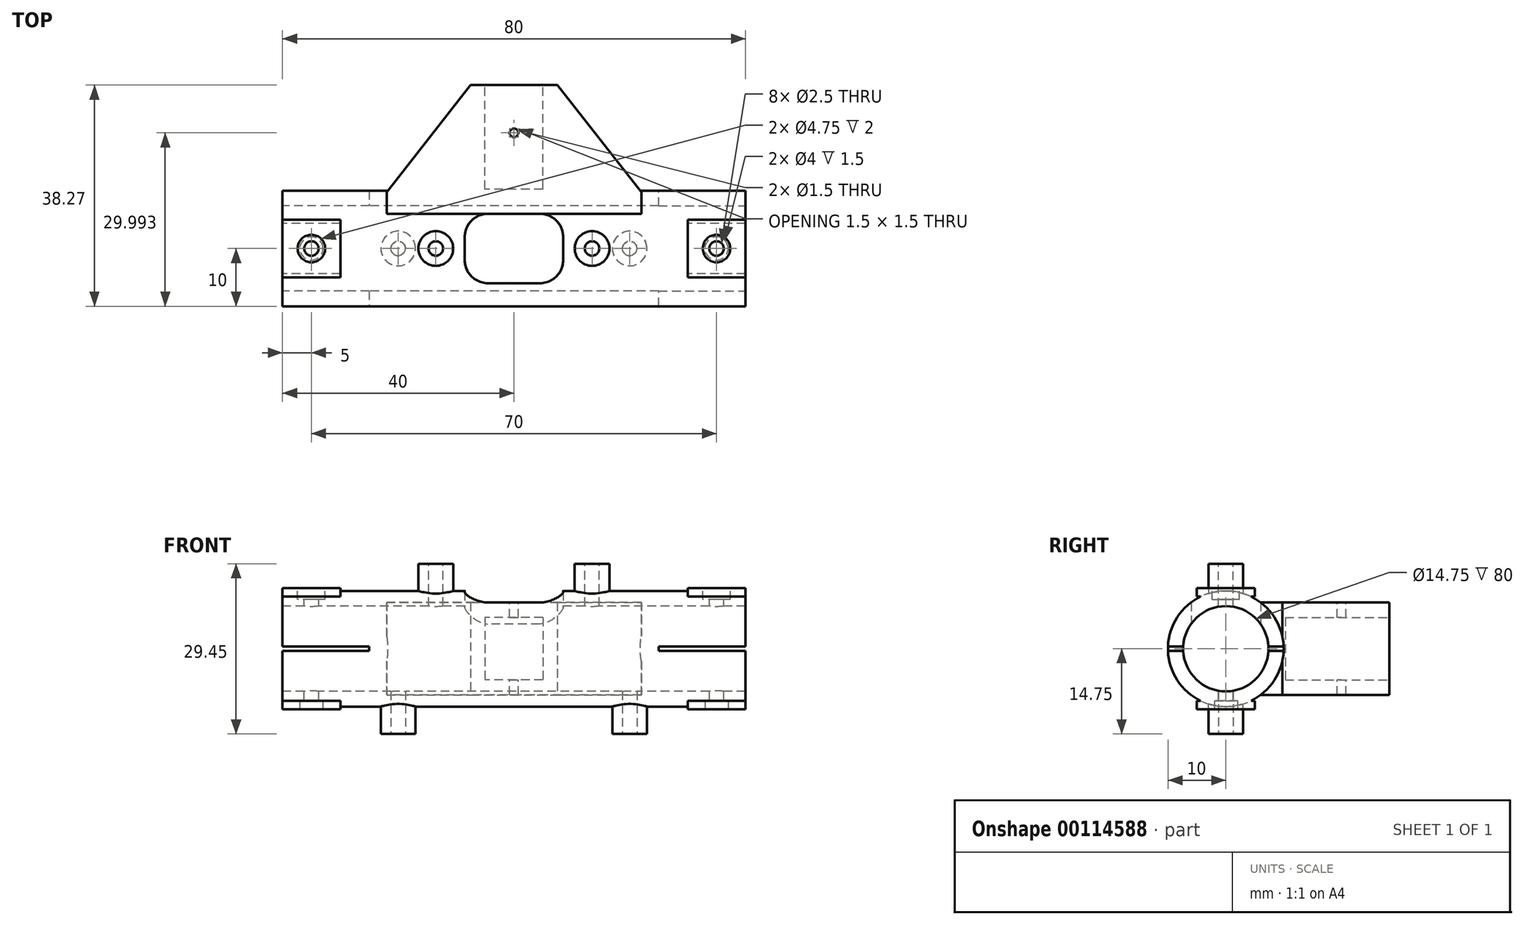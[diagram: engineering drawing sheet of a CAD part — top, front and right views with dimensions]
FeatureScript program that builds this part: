
annotation { "Feature Type Name" : "Feature", "Feature Type Description" : "" }
export const myFeature = defineFeature(function(context is Context, id is Id, definition is map)
    precondition{}
    {
        {
            var Q0;
            Q0=qCreatedBy(makeId("Right.planeOp"),FACE);
            var sketch = newSketch(context, id + "F0", { "sketchPlane" : qUnion([Q0])});
            skCircle(sketch, "E0", {"center": v(0, 0) * mm, "radius": 7.38 * mm});
            skCircle(sketch, "E1", {"center": v(0, 0) * mm, "radius": 10 * mm});
            skSolve(sketch);
        }
        {
            var Q0;
            Q0=makeQuery(id+"F0.imprint","IMPRINT",FACE,{"disambiguationData":[TD([[makeQuery(id+"F0.imprint","IMPRINT",EDGE,{"derivedFrom":sQuery(id+"F0.wireOp",EDGE,"E0")}),-1.0]])]});
            extrude(context, id + "F1", {"entities" : qUnion([Q0]), "endBound" : BoundingType.SYMMETRIC, "depth" : 80 * mm});
        }
        {
            var Q0;
            Q0=qCreatedBy(makeId("Top.planeOp"),FACE);
            var sketch = newSketch(context, id + "F2", { "sketchPlane" : qUnion([Q0])});
            skLineSegment(sketch, "E2", {"start": v(-22, 9.77) * mm, "end": v(-7.5, 28.27) * mm});
            skLineSegment(sketch, "E3", {"start": v(-7.5, 28.27) * mm, "end": v(7.5, 28.27) * mm});
            skLineSegment(sketch, "E4", {"start": v(7.5, 28.27) * mm, "end": v(22, 9.77) * mm});
            skLineSegment(sketch, "E5", {"start": v(-22, 9.77) * mm, "end": v(22, 9.77) * mm});
            skSolve(sketch);
        }
        {
            var Q0;
            Q0=makeQuery(id+"F2.imprint","IMPRINT",FACE,{"disambiguationData":[TD([[makeQuery(id+"F2.imprint","IMPRINT",EDGE,{"derivedFrom":sQuery(id+"F2.wireOp",EDGE,"E2")}),-1.0]])]});
            extrude(context, id + "F3", {"entities" : qUnion([Q0]), "operationType" : NewBodyOperationType.ADD, "endBound" : BoundingType.SYMMETRIC, "depth" : 16 * mm});
        }
        {
            var Q0;
            {var subQ0=sQuery(id+"F2.wireOp",EDGE,"E2");var subQ1=sQuery(id+"F2.wireOp",EDGE,"E5");var subQ2=sQuery(id+"F2.wireOp",EDGE,"E4");Q0=makeQuery(id+"F3.boolean.opBoolean","SPLIT",FACE,{"disambiguationData":[TD([makeQuery(id+"F3.opExtrude","CAP_FACE",FACE,{"disambiguationData":[OSD([subQ0,sQuery(id+"F2.wireOp",EDGE,"E3"),subQ2,subQ1])],"isStart":false})])],"derivedFrom":makeQuery(id+"F3.opExtrude","SWEPT_FACE",FACE,{"disambiguationData":[OSD([subQ1])]})});}
            var sketch = newSketch(context, id + "F4", { "sketchPlane" : qUnion([Q0])});
            skLineSegment(sketch, "E6.bottom", {"start": v(22, 2.15) * mm, "end": v(-22, 2.15) * mm});
            skLineSegment(sketch, "E6.top", {"start": v(22, 8) * mm, "end": v(-22, 8) * mm});
            skLineSegment(sketch, "E6.left", {"start": v(22, 2.15) * mm, "end": v(22, 8) * mm});
            skLineSegment(sketch, "E6.right", {"start": v(-22, 2.15) * mm, "end": v(-22, 8) * mm});
            skSolve(sketch);
        }
        {
            var Q0;
            {var subQ0=sQuery(id+"F2.wireOp",EDGE,"E2");var subQ1=sQuery(id+"F2.wireOp",EDGE,"E5");var subQ2=sQuery(id+"F2.wireOp",EDGE,"E4");Q0=makeQuery(id+"F3.boolean.opBoolean","SPLIT",FACE,{"disambiguationData":[TD([makeQuery(id+"F3.opExtrude","CAP_FACE",FACE,{"disambiguationData":[OSD([subQ0,sQuery(id+"F2.wireOp",EDGE,"E3"),subQ2,subQ1])],"isStart":true})])],"derivedFrom":makeQuery(id+"F3.opExtrude","SWEPT_FACE",FACE,{"disambiguationData":[OSD([subQ1])]})});}
            var sketch = newSketch(context, id + "F5", { "sketchPlane" : qUnion([Q0])});
            skLineSegment(sketch, "E7.bottom", {"start": v(22, -2.15) * mm, "end": v(-22, -2.15) * mm});
            skLineSegment(sketch, "E7.top", {"start": v(22, -8) * mm, "end": v(-22, -8) * mm});
            skLineSegment(sketch, "E7.left", {"start": v(22, -2.15) * mm, "end": v(22, -8) * mm});
            skLineSegment(sketch, "E7.right", {"start": v(-22, -2.15) * mm, "end": v(-22, -8) * mm});
            skSolve(sketch);
        }
        {
            var Q0;
            Q0=makeQuery(id+"F4.imprint","IMPRINT",FACE,{"disambiguationData":[TD([[makeQuery(id+"F4.imprint","IMPRINT",EDGE,{"derivedFrom":sQuery(id+"F4.wireOp",EDGE,"E6.bottom")}),1.0]])]});
            var Q1;
            Q1=makeQuery(id+"F5.imprint","IMPRINT",FACE,{"disambiguationData":[TD([[makeQuery(id+"F5.imprint","IMPRINT",EDGE,{"derivedFrom":sQuery(id+"F5.wireOp",EDGE,"E7.bottom")}),1.0]])]});
            extrude(context, id + "F6", {"entities" : qUnion([Q0, Q1]), "operationType" : NewBodyOperationType.ADD, "depth" : 10 * mm});
        }
        {
            var Q0;
            Q0=makeQuery(id+"F3.opExtrude","SWEPT_FACE",FACE,{"disambiguationData":[OSD([sQuery(id+"F2.wireOp",EDGE,"E3")])]});
            var sketch = newSketch(context, id + "F7", { "sketchPlane" : qUnion([Q0])});
            skLineSegment(sketch, "E8.bottom", {"start": v(-5, 5.38) * mm, "end": v(5, 5.38) * mm});
            skLineSegment(sketch, "E8.top", {"start": v(-5, -5.38) * mm, "end": v(5, -5.38) * mm});
            skLineSegment(sketch, "E8.left", {"start": v(-5, 5.38) * mm, "end": v(-5, -5.38) * mm});
            skLineSegment(sketch, "E8.right", {"start": v(5, 5.38) * mm, "end": v(5, -5.38) * mm});
            skPoint(sketch, "E8.middle", {"position": v(0, 0) * mm});
            skPoint(sketch, "E8.middle.positionSnap0", {"position": v(0, 8) * mm});
            skPoint(sketch, "E8.middle.positionSnap1", {"position": v(-7.5, 0) * mm});
            skPoint(sketch, "E8.centerSnap0", {"position": v(0, 8) * mm});
            skPoint(sketch, "E8.centerSnap1", {"position": v(-7.5, 0) * mm});
            skSolve(sketch);
        }
        {
            var Q0;
            Q0=makeQuery(id+"F7.imprint","IMPRINT",FACE,{"disambiguationData":[TD([[makeQuery(id+"F7.imprint","IMPRINT",EDGE,{"derivedFrom":sQuery(id+"F7.wireOp",EDGE,"E8.bottom")}),-1.0]])]});
            extrude(context, id + "F8", {"entities" : qUnion([Q0]), "operationType" : NewBodyOperationType.REMOVE, "oppositeDirection" : true, "depth" : 18 * mm});
        }
        {
            var Q0;
            Q0=qCreatedBy(makeId("Top.planeOp"),FACE);
            cPlane(context, id + "F9", {"entities" : qUnion([Q0]), "cplaneType" : CPlaneType.OFFSET, "offset" : 9 * mm, "width" : 150 * mm, "height" : 150 * mm});
        }
        {
            var Q0;
            Q0=qCreatedBy(id+"F9.planeOp",FACE);
            var sketch = newSketch(context, id + "F10", { "sketchPlane" : qUnion([Q0])});
            skLineSegment(sketch, "E9.bottom", {"start": v(-40, 5) * mm, "end": v(-30, 5) * mm});
            skLineSegment(sketch, "E9.top", {"start": v(-40, -5) * mm, "end": v(-30, -5) * mm});
            skLineSegment(sketch, "E9.left", {"start": v(-40, 5) * mm, "end": v(-40, -5) * mm});
            skLineSegment(sketch, "E9.right", {"start": v(-30, 5) * mm, "end": v(-30, -5) * mm});
            skLineSegment(sketch, "E10.MirrorCS", {"start": v(40, 5) * mm, "end": v(30, 5) * mm});
            skLineSegment(sketch, "E11.MirrorCS", {"start": v(40, -5) * mm, "end": v(30, -5) * mm});
            skLineSegment(sketch, "E12.MirrorCS", {"start": v(30, 5) * mm, "end": v(30, -5) * mm});
            skLineSegment(sketch, "E13.MirrorCS", {"start": v(40, 5) * mm, "end": v(40, -5) * mm});
            skSolve(sketch);
        }
        {
            var Q0;
            Q0 = qSketchRegion(id + "F10", true);
            extrude(context, id + "F11", {"entities" : qUnion([Q0]), "operationType" : NewBodyOperationType.ADD, "depth" : 1.5 * mm});
        }
        {
            var Q0;
            Q0=qCreatedBy(makeId("Top.planeOp"),FACE);
            cPlane(context, id + "F12", {"entities" : qUnion([Q0]), "cplaneType" : CPlaneType.OFFSET, "offset" : 9 * mm, "oppositeDirection" : true, "width" : 150 * mm, "height" : 150 * mm});
        }
        {
            var Q0;
            Q0=qCreatedBy(id+"F12.planeOp",FACE);
            var sketch = newSketch(context, id + "F13", { "sketchPlane" : qUnion([Q0])});
            skLineSegment(sketch, "E14.bottom", {"start": v(-40, -5) * mm, "end": v(-30, -5) * mm});
            skLineSegment(sketch, "E14.top", {"start": v(-40, 5) * mm, "end": v(-30, 5) * mm});
            skLineSegment(sketch, "E14.left", {"start": v(-40, -5) * mm, "end": v(-40, 5) * mm});
            skLineSegment(sketch, "E14.right", {"start": v(-30, -5) * mm, "end": v(-30, 5) * mm});
            skLineSegment(sketch, "E15.MirrorCS", {"start": v(30, -5) * mm, "end": v(30, 5) * mm});
            skLineSegment(sketch, "E16.MirrorCS", {"start": v(40, -5) * mm, "end": v(40, 5) * mm});
            skLineSegment(sketch, "E17.MirrorCS", {"start": v(40, -5) * mm, "end": v(30, -5) * mm});
            skLineSegment(sketch, "E18.MirrorCS", {"start": v(40, 5) * mm, "end": v(30, 5) * mm});
            skSolve(sketch);
        }
        {
            var Q0;
            Q0 = qSketchRegion(id + "F13", true);
            extrude(context, id + "F14", {"entities" : qUnion([Q0]), "operationType" : NewBodyOperationType.ADD, "oppositeDirection" : true, "depth" : 1.5 * mm});
        }
        {
            var Q0;
            Q0=qCreatedBy(id+"F9.planeOp",FACE);
            var sketch = newSketch(context, id + "F15", { "sketchPlane" : qUnion([Q0])});
            skCircle(sketch, "E19", {"center": v(-13.5, 0) * mm, "radius": 3 * mm});
            skCircle(sketch, "E20.MirrorC", {"center": v(13.5, 0) * mm, "radius": 3 * mm});
            skSolve(sketch);
        }
        {
            var Q0;
            Q0 = qSketchRegion(id + "F15", true);
            extrude(context, id + "F16", {"entities" : qUnion([Q0]), "operationType" : NewBodyOperationType.ADD, "depth" : 5.7 * mm});
        }
        {
            var Q0;
            Q0=makeQuery(id+"F11.opExtrude","CAP_FACE",FACE,{"disambiguationData":[OSD([sQuery(id+"F10.wireOp",EDGE,"E9.bottom"),sQuery(id+"F10.wireOp",EDGE,"E9.top"),sQuery(id+"F10.wireOp",EDGE,"E9.left"),sQuery(id+"F10.wireOp",EDGE,"E9.right")])],"isStart":false});
            var sketch = newSketch(context, id + "F17", { "sketchPlane" : qUnion([Q0])});
            skPoint(sketch, "E21", {"position": v(-35, 0) * mm});
            skPoint(sketch, "E21.positionSnap0", {"position": v(-40, 0) * mm});
            skPoint(sketch, "E22.MirrorP", {"position": v(35, 0) * mm});
            skSolve(sketch);
        }
        {
            var Q0;
            Q0=sQuery(id+"F17.wireOp",VERTEX,"E21");
            var Q1;
            Q1=sQuery(id+"F17.wireOp",VERTEX,"E22.MirrorP");
            var Q2;
            Q2=makeQuery(id+"F1.opExtrude","SWEPT_BODY",BODY,{"disambiguationData":[OSD([sQuery(id+"F0.wireOp",EDGE,"E0"),sQuery(id+"F0.wireOp",EDGE,"E1")])]});
            hole(context, id + "F18", {"style" : HoleStyle.C_BORE, "endStyle" : HoleEndStyle.THROUGH, "holeDiameter" : 2.5 * mm, "cBoreDiameter" : 4.75 * mm, "cBoreDepth" : 2 * mm, "locations" : qUnion([Q0, Q1]), "scope" : qUnion([Q2]), "isTappedThrough" : true});
        }
        {
            var Q0;
            Q0=makeQuery(id+"F16.opExtrude","CAP_FACE",FACE,{"disambiguationData":[OSD([sQuery(id+"F15.wireOp",EDGE,"E19")])],"isStart":false});
            var sketch = newSketch(context, id + "F19", { "sketchPlane" : qUnion([Q0])});
            skPoint(sketch, "E23", {"position": v(-13.5, 0) * mm});
            skPoint(sketch, "E24", {"position": v(87, 7.49) * mm});
            skPoint(sketch, "E25.MirrorP", {"position": v(13.5, 0) * mm});
            skSolve(sketch);
        }
        {
            var Q0;
            Q0=sQuery(id+"F19.wireOp",VERTEX,"E23");
            var Q1;
            Q1=sQuery(id+"F19.wireOp",VERTEX,"E25.MirrorP");
            var Q2;
            Q2=makeQuery(id+"F1.opExtrude","SWEPT_BODY",BODY,{"disambiguationData":[OSD([sQuery(id+"F0.wireOp",EDGE,"E0"),sQuery(id+"F0.wireOp",EDGE,"E1")])]});
            hole(context, id + "F20", {"style" : HoleStyle.SIMPLE, "endStyle" : HoleEndStyle.BLIND, "holeDiameter" : 2.5 * mm, "holeDepth" : 8 * mm, "locations" : qUnion([Q0, Q1]), "scope" : qUnion([Q2])});
        }
        {
            var Q0;
            Q0=qCreatedBy(id+"F12.planeOp",FACE);
            var sketch = newSketch(context, id + "F21", { "sketchPlane" : qUnion([Q0])});
            skCircle(sketch, "E26", {"center": v(-20, 0) * mm, "radius": 3 * mm});
            skCircle(sketch, "E27.MirrorC", {"center": v(20, 0) * mm, "radius": 3 * mm});
            skSolve(sketch);
        }
        {
            var Q0;
            Q0 = qSketchRegion(id + "F21", true);
            extrude(context, id + "F22", {"entities" : qUnion([Q0]), "operationType" : NewBodyOperationType.ADD, "oppositeDirection" : true, "depth" : 5.75 * mm});
        }
        {
            var Q0;
            Q0=makeQuery(id+"F22.opExtrude","CAP_FACE",FACE,{"disambiguationData":[OSD([sQuery(id+"F21.wireOp",EDGE,"E26")])],"isStart":false});
            var sketch = newSketch(context, id + "F23", { "sketchPlane" : qUnion([Q0])});
            skPoint(sketch, "E28", {"position": v(-20, 0) * mm});
            skPoint(sketch, "E29.MirrorP", {"position": v(20, 0) * mm});
            skSolve(sketch);
        }
        {
            var Q0;
            Q0=sQuery(id+"F23.wireOp",VERTEX,"E28");
            var Q1;
            Q1=sQuery(id+"F23.wireOp",VERTEX,"E29.MirrorP");
            var Q2;
            Q2=makeQuery(id+"F1.opExtrude","SWEPT_BODY",BODY,{"disambiguationData":[OSD([sQuery(id+"F0.wireOp",EDGE,"E0"),sQuery(id+"F0.wireOp",EDGE,"E1")])]});
            hole(context, id + "F24", {"style" : HoleStyle.SIMPLE, "endStyle" : HoleEndStyle.BLIND, "holeDiameter" : 2.5 * mm, "holeDepth" : 8 * mm, "locations" : qUnion([Q0, Q1]), "scope" : qUnion([Q2])});
        }
        {
            var Q0;
            Q0=makeQuery(id+"F14.boolean.opBoolean","MERGE",FACE,{"derivedFrom":[makeQuery(id+"F11.boolean.opBoolean","MERGE",FACE,{"derivedFrom":[makeQuery(id+"F1.opExtrude","CAP_FACE",FACE,{"disambiguationData":[OSD([sQuery(id+"F0.wireOp",EDGE,"E0"),sQuery(id+"F0.wireOp",EDGE,"E1")])],"isStart":false}),makeQuery(id+"F11.opExtrude","SWEPT_FACE",FACE,{"disambiguationData":[OSD([sQuery(id+"F10.wireOp",EDGE,"E13.MirrorCS")])]})]}),makeQuery(id+"F14.opExtrude","SWEPT_FACE",FACE,{"disambiguationData":[OSD([sQuery(id+"F13.wireOp",EDGE,"E16.MirrorCS")])]})]});
            var sketch = newSketch(context, id + "F25", { "sketchPlane" : qUnion([Q0])});
            skCircle(sketch, "E30.0", {"center": v(0, 0) * mm, "radius": 7.38 * mm});
            skSolve(sketch);
        }
        {
            var Q0;
            Q0 = qSketchRegion(id + "F25", true);
            extrude(context, id + "F26", {"entities" : qUnion([Q0]), "operationType" : NewBodyOperationType.REMOVE, "endBound" : BoundingType.THROUGH_ALL, "oppositeDirection" : true, "depth" : 25 * mm});
        }
        {
            var Q0;
            Q0=makeQuery(id+"F14.opExtrude","CAP_FACE",FACE,{"disambiguationData":[OSD([sQuery(id+"F13.wireOp",EDGE,"E15.MirrorCS"),sQuery(id+"F13.wireOp",EDGE,"E16.MirrorCS"),sQuery(id+"F13.wireOp",EDGE,"E17.MirrorCS"),sQuery(id+"F13.wireOp",EDGE,"E18.MirrorCS")])],"isStart":false});
            var sketch = newSketch(context, id + "F27", { "sketchPlane" : qUnion([Q0])});
            skCircle(sketch, "E31", {"center": v(35, 0) * mm, "radius": 2 * mm});
            skCircle(sketch, "E32.MirrorC", {"center": v(-35, 0) * mm, "radius": 2 * mm});
            skSolve(sketch);
        }
        {
            var Q0;
            Q0 = qSketchRegion(id + "F27", true);
            extrude(context, id + "F28", {"entities" : qUnion([Q0]), "operationType" : NewBodyOperationType.REMOVE, "oppositeDirection" : true, "depth" : 1.5 * mm});
        }
        {
            var Q0;
            Q0=qCreatedBy(makeId("Top.planeOp"),FACE);
            var sketch = newSketch(context, id + "F29", { "sketchPlane" : qUnion([Q0])});
            skLineSegment(sketch, "E33.bottom", {"start": v(-8.5, 6) * mm, "end": v(8.5, 6) * mm});
            skLineSegment(sketch, "E33.top", {"start": v(-8.5, -6) * mm, "end": v(8.5, -6) * mm});
            skLineSegment(sketch, "E33.left", {"start": v(-8.5, 6) * mm, "end": v(-8.5, -6) * mm});
            skLineSegment(sketch, "E33.right", {"start": v(8.5, 6) * mm, "end": v(8.5, -6) * mm});
            skPoint(sketch, "E33.middle", {"position": v(0, 0) * mm});
            skSolve(sketch);
        }
        {
            var Q0;
            Q0 = qSketchRegion(id + "F29", true);
            extrude(context, id + "F30", {"entities" : qUnion([Q0]), "operationType" : NewBodyOperationType.REMOVE, "depth" : 25 * mm});
        }
        {
            var Q0;
            Q0=makeQuery(id+"F30.boolean.opBoolean","COPY",EDGE,{"derivedFrom":makeQuery(id+"F30.opExtrude","SWEPT_EDGE",EDGE,{"disambiguationData":[OSD([sQuery(id+"F29.wireOp",EDGE,"E33.bottom"),sQuery(id+"F29.wireOp",EDGE,"E33.right")])]})});
            var Q1;
            Q1=makeQuery(id+"F30.boolean.opBoolean","COPY",EDGE,{"derivedFrom":makeQuery(id+"F30.opExtrude","SWEPT_EDGE",EDGE,{"disambiguationData":[OSD([sQuery(id+"F29.wireOp",EDGE,"E33.bottom"),sQuery(id+"F29.wireOp",EDGE,"E33.left")])]})});
            var Q2;
            Q2=makeQuery(id+"F30.boolean.opBoolean","COPY",EDGE,{"derivedFrom":makeQuery(id+"F30.opExtrude","SWEPT_EDGE",EDGE,{"disambiguationData":[OSD([sQuery(id+"F29.wireOp",EDGE,"E33.top"),sQuery(id+"F29.wireOp",EDGE,"E33.left")])]})});
            var Q3;
            Q3=makeQuery(id+"F30.boolean.opBoolean","COPY",EDGE,{"derivedFrom":makeQuery(id+"F30.opExtrude","SWEPT_EDGE",EDGE,{"disambiguationData":[OSD([sQuery(id+"F29.wireOp",EDGE,"E33.top"),sQuery(id+"F29.wireOp",EDGE,"E33.right")])]})});
            fillet(context, id + "F31", {"entities" : qUnion([Q0, Q1, Q2, Q3]), "radius" : 4 * mm, "tangentPropagation" : true, "allowEdgeOverflow" : false});
        }
        {
            var Q0;
            Q0=makeQuery(id+"F14.boolean.opBoolean","MERGE",FACE,{"derivedFrom":[makeQuery(id+"F11.boolean.opBoolean","MERGE",FACE,{"derivedFrom":[makeQuery(id+"F1.opExtrude","CAP_FACE",FACE,{"disambiguationData":[OSD([sQuery(id+"F0.wireOp",EDGE,"E0"),sQuery(id+"F0.wireOp",EDGE,"E1")])],"isStart":false}),makeQuery(id+"F11.opExtrude","SWEPT_FACE",FACE,{"disambiguationData":[OSD([sQuery(id+"F10.wireOp",EDGE,"E13.MirrorCS")])]})]}),makeQuery(id+"F14.opExtrude","SWEPT_FACE",FACE,{"disambiguationData":[OSD([sQuery(id+"F13.wireOp",EDGE,"E16.MirrorCS")])]})]});
            var sketch = newSketch(context, id + "F32", { "sketchPlane" : qUnion([Q0])});
            skLineSegment(sketch, "E34.bottom", {"start": v(-12.5, 0.37) * mm, "end": v(12.5, 0.38) * mm});
            skLineSegment(sketch, "E34.top", {"start": v(-12.5, -0.38) * mm, "end": v(12.5, -0.37) * mm});
            skLineSegment(sketch, "E34.left", {"start": v(-12.5, 0.37) * mm, "end": v(-12.5, -0.38) * mm});
            skLineSegment(sketch, "E34.right", {"start": v(12.5, 0.38) * mm, "end": v(12.5, -0.37) * mm});
            skSolve(sketch);
        }
        {
            var Q0;
            {var subQ0=sQuery(id+"F32.wireOp",EDGE,"E34.bottom");var subQ1=makeQuery(id+"F14.boolean.opBoolean","SPLIT",EDGE,{"disambiguationData":[OD(0.0)],"derivedFrom":makeQuery(id+"F1.opExtrude","CAP_EDGE",EDGE,{"disambiguationData":[OSD([sQuery(id+"F0.wireOp",EDGE,"E1")])],"isStart":false})});var subQ2=makeQuery(id+"F32.imprint","INTERSECT",VERTEX,{"derivedFrom":[subQ1,subQ0]});Q0=makeQuery(id+"F32.imprint","IMPRINT",FACE,{"disambiguationData":[TD([[makeQuery(id+"F32.imprint","IMPRINT",EDGE,{"disambiguationData":[TD([[subQ2,1.0]])],"derivedFrom":subQ0}),-1.0]])]});}
            var Q1;
            {var subQ0=sQuery(id+"F32.wireOp",EDGE,"E34.bottom");var subQ1=makeQuery(id+"F14.boolean.opBoolean","SPLIT",EDGE,{"disambiguationData":[OD(1.0)],"derivedFrom":makeQuery(id+"F1.opExtrude","CAP_EDGE",EDGE,{"disambiguationData":[OSD([sQuery(id+"F0.wireOp",EDGE,"E1")])],"isStart":false})});var subQ2=makeQuery(id+"F32.imprint","INTERSECT",VERTEX,{"derivedFrom":[subQ1,subQ0]});Q1=makeQuery(id+"F32.imprint","IMPRINT",FACE,{"disambiguationData":[TD([[makeQuery(id+"F32.imprint","IMPRINT",EDGE,{"disambiguationData":[TD([[subQ2,-1.0]])],"derivedFrom":subQ0}),-1.0]])]});}
            extrude(context, id + "F33", {"entities" : qUnion([Q0, Q1]), "operationType" : NewBodyOperationType.REMOVE, "oppositeDirection" : true, "depth" : 15 * mm});
        }
        {
            var Q0;
            Q0=makeQuery(id+"F14.boolean.opBoolean","MERGE",FACE,{"derivedFrom":[makeQuery(id+"F11.boolean.opBoolean","MERGE",FACE,{"derivedFrom":[makeQuery(id+"F1.opExtrude","CAP_FACE",FACE,{"disambiguationData":[OSD([sQuery(id+"F0.wireOp",EDGE,"E0"),sQuery(id+"F0.wireOp",EDGE,"E1")])],"isStart":true}),makeQuery(id+"F11.opExtrude","SWEPT_FACE",FACE,{"disambiguationData":[OSD([sQuery(id+"F10.wireOp",EDGE,"E9.left")])]})]}),makeQuery(id+"F14.opExtrude","SWEPT_FACE",FACE,{"disambiguationData":[OSD([sQuery(id+"F13.wireOp",EDGE,"E14.left")])]})]});
            var sketch = newSketch(context, id + "F34", { "sketchPlane" : qUnion([Q0])});
            skLineSegment(sketch, "E35.bottom", {"start": v(-11.2, 0.38) * mm, "end": v(13.28, 0.38) * mm});
            skLineSegment(sketch, "E35.top", {"start": v(-11.2, -0.38) * mm, "end": v(13.28, -0.38) * mm});
            skLineSegment(sketch, "E35.left", {"start": v(-11.2, 0.38) * mm, "end": v(-11.2, -0.38) * mm});
            skLineSegment(sketch, "E35.right", {"start": v(13.28, 0.38) * mm, "end": v(13.28, -0.38) * mm});
            skSolve(sketch);
        }
        {
            var Q0;
            {var subQ0=sQuery(id+"F34.wireOp",EDGE,"E35.bottom");var subQ1=makeQuery(id+"F14.boolean.opBoolean","SPLIT",EDGE,{"disambiguationData":[OD(0.0)],"derivedFrom":makeQuery(id+"F1.opExtrude","CAP_EDGE",EDGE,{"disambiguationData":[OSD([sQuery(id+"F0.wireOp",EDGE,"E1")])],"isStart":true})});var subQ2=makeQuery(id+"F34.imprint","INTERSECT",VERTEX,{"derivedFrom":[subQ1,subQ0]});Q0=makeQuery(id+"F34.imprint","IMPRINT",FACE,{"disambiguationData":[TD([[makeQuery(id+"F34.imprint","IMPRINT",EDGE,{"disambiguationData":[TD([[subQ2,-1.0]])],"derivedFrom":subQ0}),-1.0]])]});}
            var Q1;
            {var subQ0=sQuery(id+"F34.wireOp",EDGE,"E35.bottom");var subQ1=makeQuery(id+"F14.boolean.opBoolean","SPLIT",EDGE,{"disambiguationData":[OD(1.0)],"derivedFrom":makeQuery(id+"F1.opExtrude","CAP_EDGE",EDGE,{"disambiguationData":[OSD([sQuery(id+"F0.wireOp",EDGE,"E1")])],"isStart":true})});var subQ2=makeQuery(id+"F34.imprint","INTERSECT",VERTEX,{"derivedFrom":[subQ1,subQ0]});Q1=makeQuery(id+"F34.imprint","IMPRINT",FACE,{"disambiguationData":[TD([[makeQuery(id+"F34.imprint","IMPRINT",EDGE,{"disambiguationData":[TD([[subQ2,1.0]])],"derivedFrom":subQ0}),-1.0]])]});}
            extrude(context, id + "F35", {"entities" : qUnion([Q0, Q1]), "operationType" : NewBodyOperationType.REMOVE, "oppositeDirection" : true, "depth" : 15 * mm});
        }
        {
            var Q0;
            Q0=makeQuery(id+"F6.boolean.opBoolean","MERGE",FACE,{"derivedFrom":[makeQuery(id+"F3.opExtrude","CAP_FACE",FACE,{"disambiguationData":[OSD([sQuery(id+"F2.wireOp",EDGE,"E2"),sQuery(id+"F2.wireOp",EDGE,"E3"),sQuery(id+"F2.wireOp",EDGE,"E4"),sQuery(id+"F2.wireOp",EDGE,"E5")])],"isStart":false}),makeQuery(id+"F6.opExtrude","SWEPT_FACE",FACE,{"disambiguationData":[OSD([sQuery(id+"F4.wireOp",EDGE,"E6.top")])]})]});
            var sketch = newSketch(context, id + "F36", { "sketchPlane" : qUnion([Q0])});
            skCircle(sketch, "E36", {"center": v(0, 20) * mm, "radius": 0.75 * mm});
            skPoint(sketch, "E36.centerSnap0", {"position": v(0, 28.27) * mm});
            skSolve(sketch);
        }
        {
            var Q0;
            Q0 = qSketchRegion(id + "F36", true);
            extrude(context, id + "F37", {"entities" : qUnion([Q0]), "operationType" : NewBodyOperationType.REMOVE, "oppositeDirection" : true, "depth" : 25 * mm});
        }
    });
